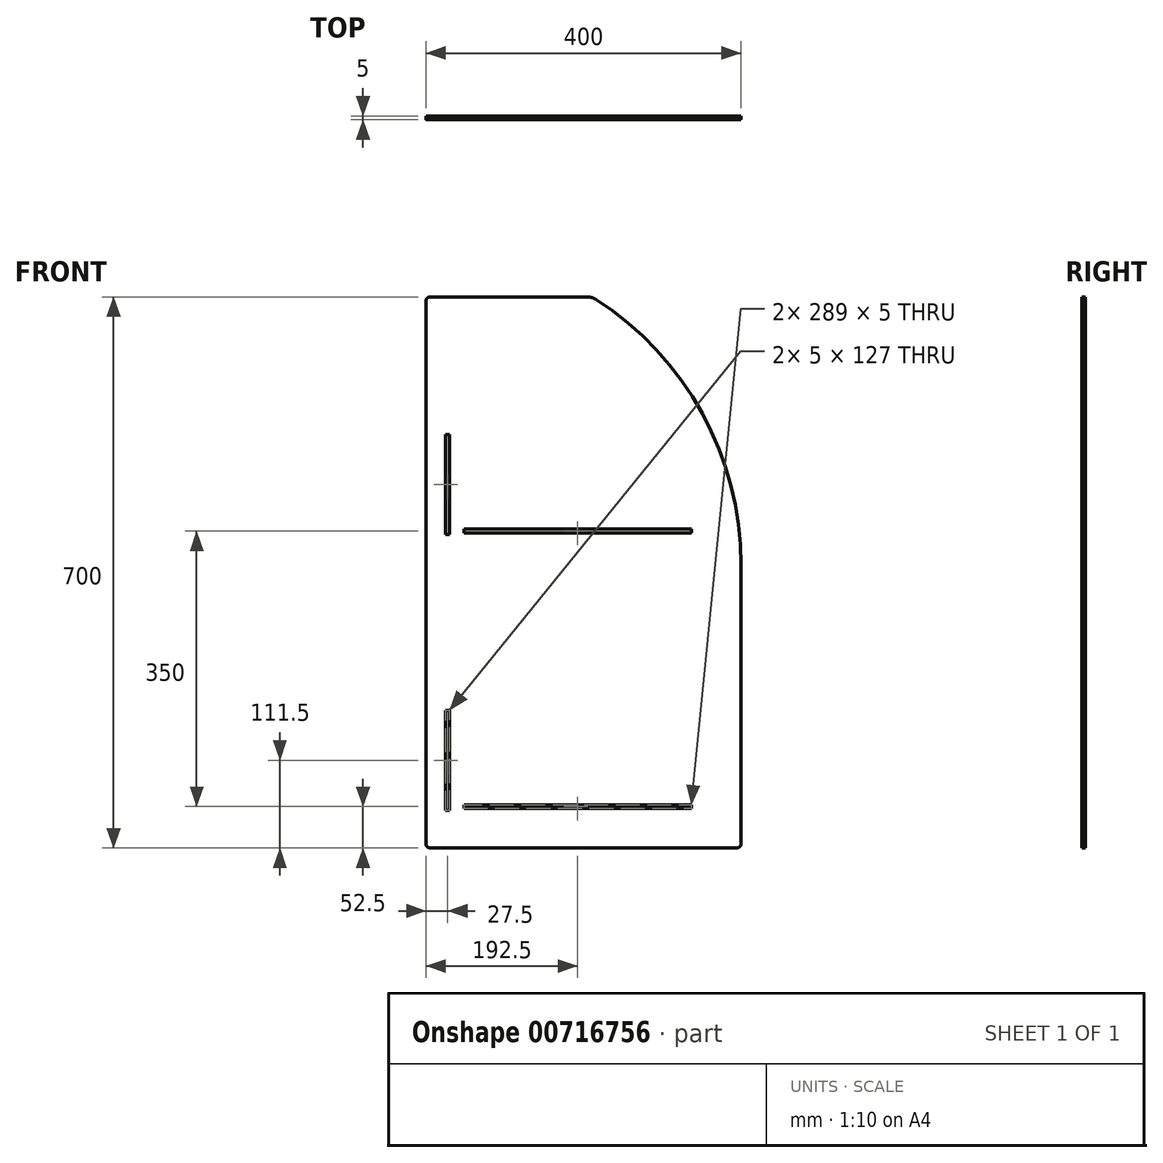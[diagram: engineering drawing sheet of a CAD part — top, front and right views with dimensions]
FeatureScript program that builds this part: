
annotation { "Feature Type Name" : "Feature", "Feature Type Description" : "" }
export const myFeature = defineFeature(function(context is Context, id is Id, definition is map)
    precondition{}
    {
        {
            var Q0;
            Q0=qCreatedBy(makeId("Front.planeOp"),FACE);
            var sketch = newSketch(context, id + "F0", { "sketchPlane" : qUnion([Q0])});
            skLineSegment(sketch, "E0.bottom", {"start": v(5, 0) * mm, "end": v(395, 0) * mm});
            skLineSegment(sketch, "E0.top", {"start": v(5, 700) * mm, "end": v(204.94, 700) * mm});
            skLineSegment(sketch, "E0.left", {"start": v(0, 5) * mm, "end": v(0, 695) * mm});
            skLineSegment(sketch, "E0.right", {"start": v(400, 5) * mm, "end": v(400, 360) * mm});
            skLineSegment(sketch, "E1.bottom", {"start": v(48, 55) * mm, "end": v(337, 55) * mm});
            skLineSegment(sketch, "E1.top", {"start": v(48, 50) * mm, "end": v(337, 50) * mm});
            skLineSegment(sketch, "E1.left", {"start": v(48, 55) * mm, "end": v(48, 50) * mm});
            skLineSegment(sketch, "E1.right", {"start": v(337, 55) * mm, "end": v(337, 50) * mm});
            skLineSegment(sketch, "E2.bottom", {"start": v(48, 405) * mm, "end": v(337, 405) * mm});
            skLineSegment(sketch, "E2.top", {"start": v(48, 400) * mm, "end": v(337, 400) * mm});
            skLineSegment(sketch, "E2.left", {"start": v(48, 400) * mm, "end": v(48, 405) * mm});
            skLineSegment(sketch, "E2.right", {"start": v(337, 400) * mm, "end": v(337, 405) * mm});
            skLineSegment(sketch, "E3.bottom", {"start": v(25, 525) * mm, "end": v(30, 525) * mm});
            skLineSegment(sketch, "E3.top", {"start": v(25, 398) * mm, "end": v(30, 398) * mm});
            skLineSegment(sketch, "E3.left", {"start": v(25, 525) * mm, "end": v(25, 398) * mm});
            skLineSegment(sketch, "E3.right", {"start": v(30, 525) * mm, "end": v(30, 398) * mm});
            skLineSegment(sketch, "E4.bottom", {"start": v(25, 175) * mm, "end": v(30, 175) * mm});
            skLineSegment(sketch, "E4.top", {"start": v(25, 48) * mm, "end": v(30, 48) * mm});
            skLineSegment(sketch, "E4.left", {"start": v(25, 175) * mm, "end": v(25, 48) * mm});
            skLineSegment(sketch, "E4.right", {"start": v(30, 175) * mm, "end": v(30, 48) * mm});
            skPoint(sketch, "E5.visualSharp", {"position": v(400, 700) * mm});
            skArc(sketch, "E6.trimOffspring", {"start": v(400, 360) * mm, "mid": v(350.92, 551.98) * mm, "end": v(215.73, 696.84) * mm});
            skPoint(sketch, "E7.center.orphan", {"position": v(-150, 360) * mm});
            skPoint(sketch, "E8.visualSharp", {"position": v(210.71, 700) * mm});
            skArc(sketch, "E8.filletArc", {"start": v(215.73, 696.84) * mm, "mid": v(210.56, 699.2) * mm, "end": v(204.94, 700) * mm});
            skPoint(sketch, "E9.visualSharp", {"position": v(0, 700) * mm});
            skArc(sketch, "E9.filletArc", {"start": v(5, 700) * mm, "mid": v(1.46, 698.54) * mm, "end": v(0, 695) * mm});
            skPoint(sketch, "E10.visualSharp", {"position": v(0, 0) * mm});
            skArc(sketch, "E10.filletArc", {"start": v(0, 5) * mm, "mid": v(1.46, 1.46) * mm, "end": v(5, 0) * mm});
            skPoint(sketch, "E11.visualSharp", {"position": v(400, 0) * mm});
            skArc(sketch, "E11.filletArc", {"start": v(395, 0) * mm, "mid": v(398.54, 1.46) * mm, "end": v(400, 5) * mm});
            skSolve(sketch);
        }
        {
            var Q0;
            Q0 = qSketchRegion(id + "F0", true);
            extrude(context, id + "F1", {"entities" : qUnion([Q0]), "depth" : 5 * mm, "offsetDistance" : 25 * mm});
        }
    });
